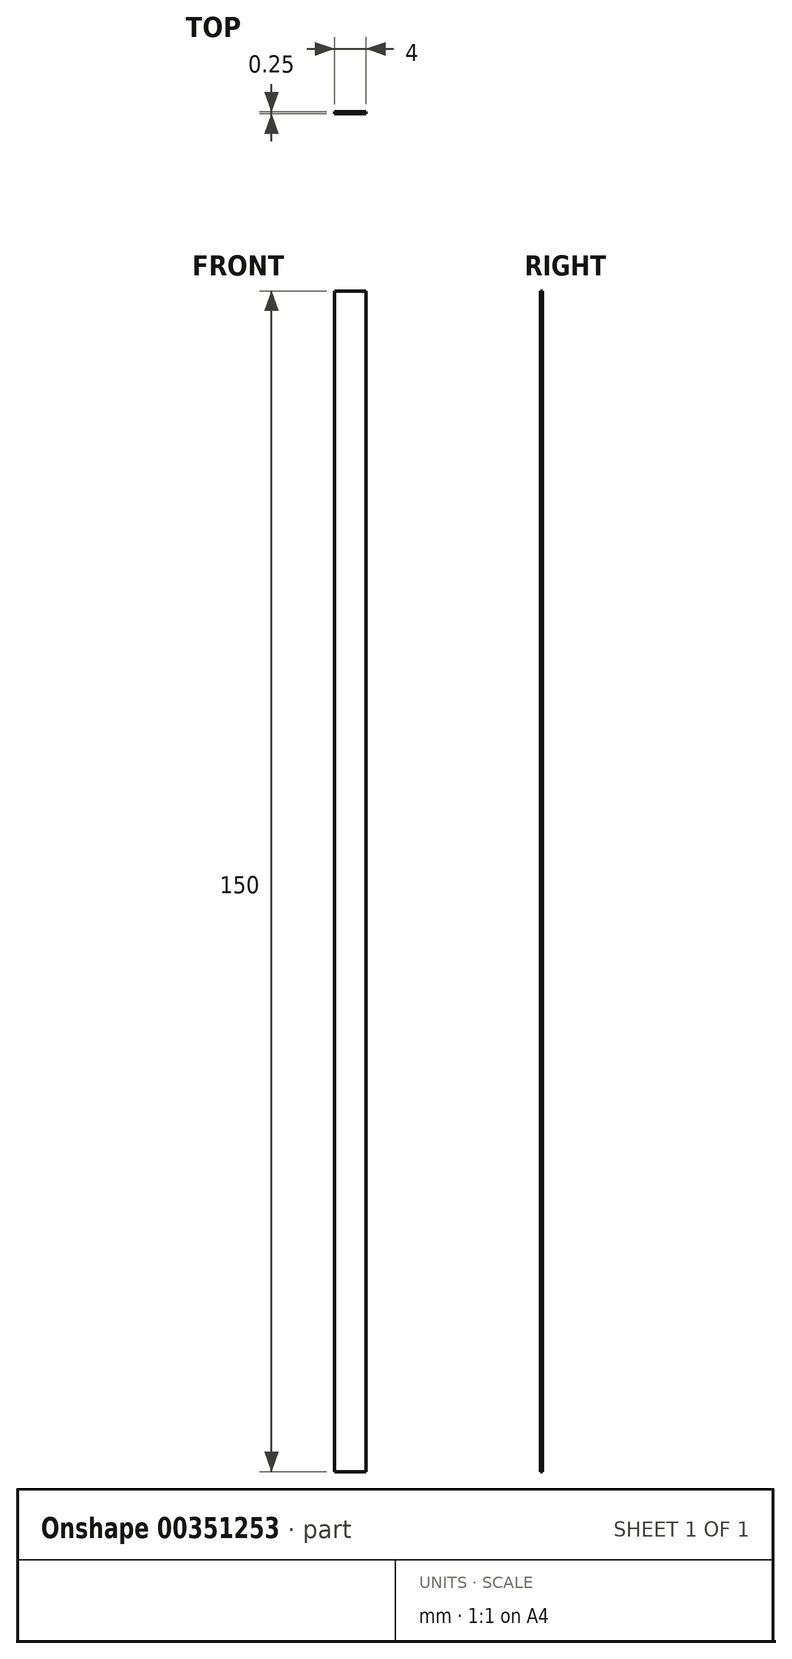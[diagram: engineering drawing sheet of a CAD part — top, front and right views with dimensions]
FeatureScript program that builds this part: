
annotation { "Feature Type Name" : "Feature", "Feature Type Description" : "" }
export const myFeature = defineFeature(function(context is Context, id is Id, definition is map)
    precondition{}
    {
        {
            var Q0;
            Q0=qCreatedBy(makeId("Front.planeOp"),FACE);
            var sketch = newSketch(context, id + "F0", { "sketchPlane" : qUnion([Q0])});
            skLineSegment(sketch, "E0.bottom", {"start": v(-33.25, 78.64) * mm, "end": v(-29.25, 78.64) * mm});
            skLineSegment(sketch, "E0.top", {"start": v(-33.25, -71.36) * mm, "end": v(-29.25, -71.36) * mm});
            skLineSegment(sketch, "E0.left", {"start": v(-33.25, 78.64) * mm, "end": v(-33.25, -71.36) * mm});
            skLineSegment(sketch, "E0.right", {"start": v(-29.25, 78.64) * mm, "end": v(-29.25, -71.36) * mm});
            skSolve(sketch);
        }
        {
            var Q0;
            Q0=makeQuery(id+"F0.imprint","IMPRINT",FACE,{"disambiguationData":[TD([[makeQuery(id+"F0.imprint","IMPRINT",EDGE,{"derivedFrom":sQuery(id+"F0.wireOp",EDGE,"E0.bottom")}),-1.0]])]});
            extrude(context, id + "F1", {"entities" : qUnion([Q0]), "depth" : 0.25 * mm});
        }
    });
